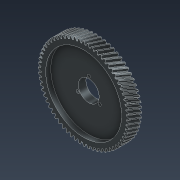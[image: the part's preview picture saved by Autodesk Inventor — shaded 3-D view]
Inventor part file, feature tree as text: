
AUTODESK INVENTOR PART (.ipt)
format: ipt  version: 2022 (Build 260153000, 153)  size: 875,520 bytes
history: native  units: mm (DEFAULTED — no unit token found)
features: sketch x5, extrude x3, plane x3, other x3, hole x1
ambient origin geometry x8: Origin, YZ Plane, XZ Plane, XY Plane, X Axis, Y Axis, Z Axis, Center Point
bodies: Solid1 (feature_tree)
feature tree (15):
  extrude  "Extrusion1"  Depth=20.0mm TaperAngle=0.0deg
  plane  "Work Plane2"
  plane  "Work Plane8"
  plane  "Work Plane9"
  other  "Spur Gear"
  extrude  "Extrusion2"  Depth=10.0mm TaperAngle=0.0deg
  extrude  "Extrusion3"  Depth=0.490874mm TaperAngle=0.0deg
  hole  "Hole1"  [1 undecoded]
  sketch  "Sketch1"  dims[d0=143.892623mm d1=20.0mm d2=0.0mm]
  sketch  "Sketch2"  dims[d3=136.214755mm d4=10.0mm d5=0.0mm]
  other  "Srf1"
  sketch  "Sketch3"  dims[d16=104.0mm d17=0.0mm d34=0.490874mm]
  sketch  "Sketch4"  dims[d39=0.0mm d41=0.0mm]
  sketch  "Sketch5"  dims[d43=104.0mm d46=104.0mm d47=0.0mm d48=0.0mm d49=120.0mm d50=8.0mm d51=0.0mm d52=33.0mm d53=0.0mm d54=0.0mm d55=40.0mm d56=30.0mm d58=360.0deg d60=5.0mm d61=5.0mm d62=4.0mm d63=2.0mm d64=90.0deg d65=5.0mm d66=0.0mm]
  other  "Pitch Diameter"
note: 1 required parameter value undecoded (feature->parameter linkage not recoverable at this tier; creation-order binding heuristic only, values carry confidence <= 0.55)
